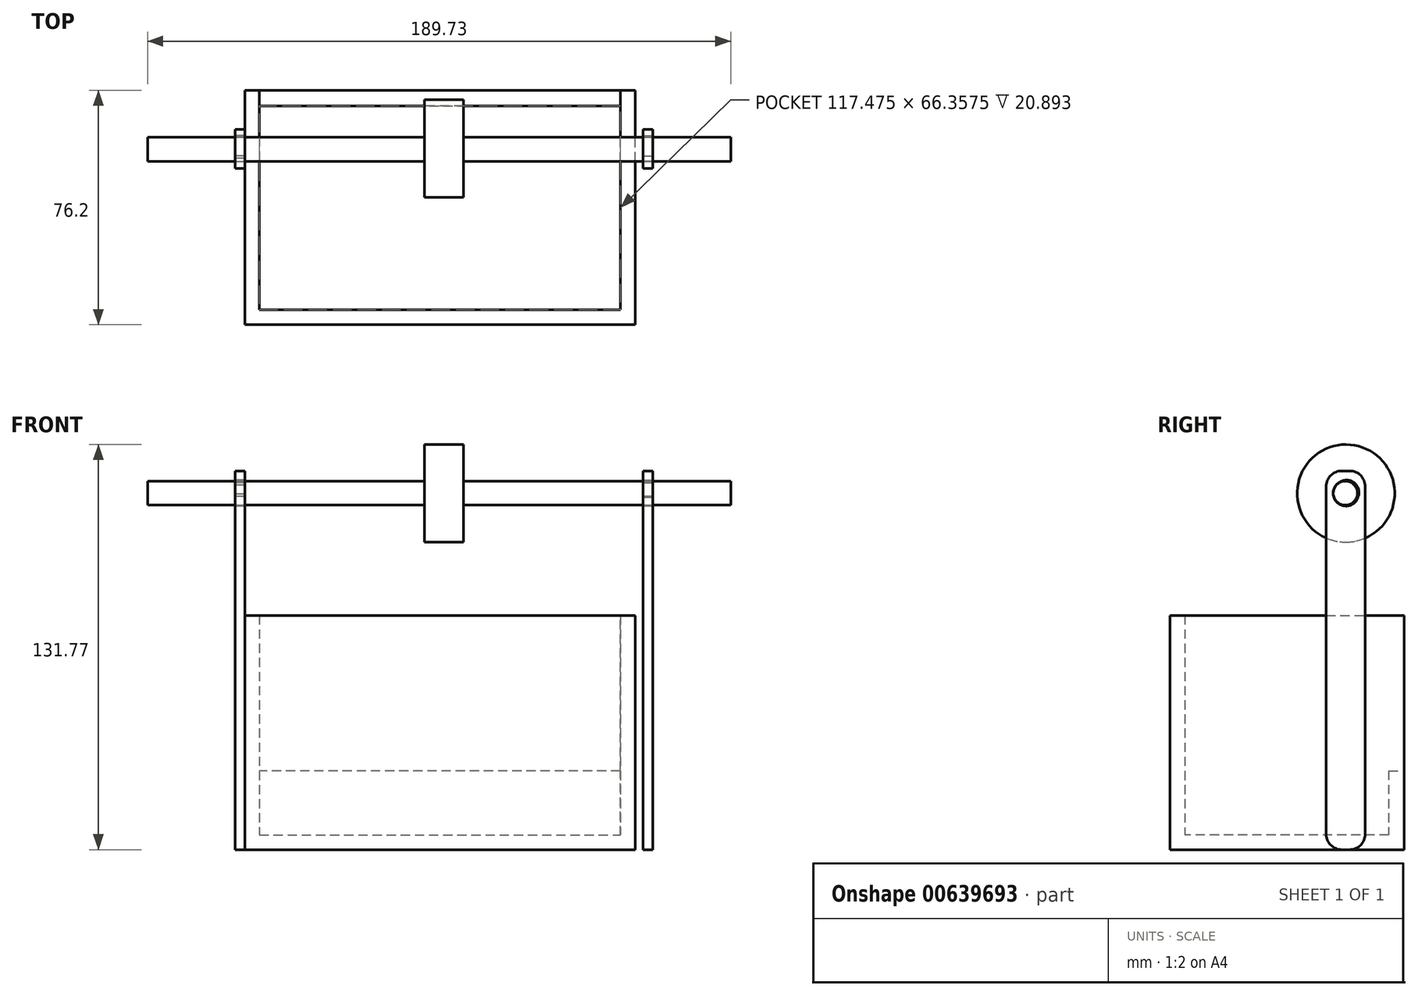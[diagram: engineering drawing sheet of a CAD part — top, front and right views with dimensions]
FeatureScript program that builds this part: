
annotation { "Feature Type Name" : "Feature", "Feature Type Description" : "" }
export const myFeature = defineFeature(function(context is Context, id is Id, definition is map)
    precondition{}
    {
        {
            var Q0;
            Q0=qCreatedBy(makeId("Top.planeOp"),FACE);
            var sketch = newSketch(context, id + "F0", { "sketchPlane" : qUnion([Q0])});
            skLineSegment(sketch, "E0", {"start": v(-64.77, -58.54) * mm, "end": v(62.23, -58.54) * mm});
            skLineSegment(sketch, "E1", {"start": v(62.23, -58.54) * mm, "end": v(62.23, 43.06) * mm});
            skLineSegment(sketch, "E2", {"start": v(62.23, 43.06) * mm, "end": v(-64.77, 43.06) * mm});
            skLineSegment(sketch, "E3", {"start": v(-64.77, 43.06) * mm, "end": v(-64.77, -58.54) * mm});
            skSolve(sketch);
        }
        {
            var Q0;
            Q0=makeQuery(id+"F0.imprint","IMPRINT",FACE,{"disambiguationData":[TD([[makeQuery(id+"F0.imprint","IMPRINT",EDGE,{"derivedFrom":sQuery(id+"F0.wireOp",EDGE,"E0")}),1.0]])]});
            extrude(context, id + "F1", {"entities" : qUnion([Q0]), "depth" : 76.2 * mm, "offsetDistance" : 25.4 * mm});
        }
        {
            var Q0;
            Q0=makeQuery(id+"F1.opExtrude","CAP_FACE",FACE,{"disambiguationData":[OSD([sQuery(id+"F0.wireOp",EDGE,"E0"),sQuery(id+"F0.wireOp",EDGE,"E1"),sQuery(id+"F0.wireOp",EDGE,"E2"),sQuery(id+"F0.wireOp",EDGE,"E3")])],"isStart":false});
            shell(context, id + "F2", {"entities" : qUnion([Q0]), "thickness" : 4.76 * mm});
        }
        {
            var Q0;
            Q0=makeQuery(id+"F1.opExtrude","CAP_FACE",FACE,{"disambiguationData":[OSD([sQuery(id+"F0.wireOp",EDGE,"E0"),sQuery(id+"F0.wireOp",EDGE,"E1"),sQuery(id+"F0.wireOp",EDGE,"E2"),sQuery(id+"F0.wireOp",EDGE,"E3")])],"isStart":true});
            var sketch = newSketch(context, id + "F3", { "sketchPlane" : qUnion([Q0])});
            skLineSegment(sketch, "E4.bottom", {"start": v(-64.77, 7.74) * mm, "end": v(-67.94, 7.74) * mm});
            skLineSegment(sketch, "E4.top", {"start": v(-64.77, -4.96) * mm, "end": v(-67.94, -4.96) * mm});
            skLineSegment(sketch, "E4.left", {"start": v(-64.77, 7.74) * mm, "end": v(-64.77, -4.96) * mm});
            skLineSegment(sketch, "E4.right", {"start": v(-67.94, 7.74) * mm, "end": v(-67.94, -4.96) * mm});
            skSolve(sketch);
        }
        {
            var Q0;
            Q0=makeQuery(id+"F3.imprint","IMPRINT",FACE,{"disambiguationData":[TD([[makeQuery(id+"F3.imprint","IMPRINT",EDGE,{"derivedFrom":sQuery(id+"F3.wireOp",EDGE,"E4.bottom")}),1.0]])]});
            extrude(context, id + "F4", {"entities" : qUnion([Q0]), "oppositeDirection" : true, "depth" : 123.19 * mm, "offsetDistance" : 25.4 * mm});
        }
        {
            var Q0;
            Q0=makeQuery(id+"F4.opExtrude","CAP_EDGE",EDGE,{"disambiguationData":[OSD([sQuery(id+"F3.wireOp",EDGE,"E4.bottom")])],"isStart":false});
            var Q1;
            Q1=makeQuery(id+"F4.opExtrude","CAP_EDGE",EDGE,{"disambiguationData":[OSD([sQuery(id+"F3.wireOp",EDGE,"E4.top")])],"isStart":false});
            var Q2;
            Q2=makeQuery(id+"F4.opExtrude","CAP_EDGE",EDGE,{"disambiguationData":[OSD([sQuery(id+"F3.wireOp",EDGE,"E4.bottom")])],"isStart":true});
            var Q3;
            Q3=makeQuery(id+"F4.opExtrude","CAP_EDGE",EDGE,{"disambiguationData":[OSD([sQuery(id+"F3.wireOp",EDGE,"E4.top")])],"isStart":true});
            fillet(context, id + "F5", {"entities" : qUnion([Q0, Q1, Q2, Q3]), "radius" : 5.08 * mm, "tangentPropagation" : true, "allowEdgeOverflow" : false});
        }
        {
            var Q0;
            Q0=makeQuery(id+"F4.opExtrude","SWEPT_FACE",FACE,{"disambiguationData":[OSD([sQuery(id+"F3.wireOp",EDGE,"E4.right")])]});
            var sketch = newSketch(context, id + "F6", { "sketchPlane" : qUnion([Q0])});
            skCircle(sketch, "E5", {"center": v(1.13, 116.18) * mm, "radius": 4.02 * mm});
            skSolve(sketch);
        }
        {
            var Q0;
            Q0=makeQuery(id+"F6.imprint","IMPRINT",FACE,{"disambiguationData":[TD([[makeQuery(id+"F6.imprint","IMPRINT",EDGE,{"derivedFrom":sQuery(id+"F6.wireOp",EDGE,"E5")}),1.0]])]});
            extrude(context, id + "F7", {"entities" : qUnion([Q0]), "operationType" : NewBodyOperationType.REMOVE, "oppositeDirection" : true, "depth" : 25.4 * mm, "offsetDistance" : 25.4 * mm});
        }
        {
            var Q0;
            Q0=makeQuery(id+"F4.opExtrude","SWEPT_BODY",BODY,{"disambiguationData":[OSD([sQuery(id+"F3.wireOp",EDGE,"E4.bottom"),sQuery(id+"F3.wireOp",EDGE,"E4.top"),sQuery(id+"F3.wireOp",EDGE,"E4.left"),sQuery(id+"F3.wireOp",EDGE,"E4.right")])]});
            var Q1;
            Q1=qCreatedBy(makeId("Right.planeOp"),FACE);
            mirror(context, id + "F8", {"entities" : qUnion([Q0]), "mirrorPlane" : qUnion([Q1])});
        }
        {
            var Q0;
            Q0=makeQuery(id+"F4.opExtrude","SWEPT_FACE",FACE,{"disambiguationData":[OSD([sQuery(id+"F3.wireOp",EDGE,"E4.right")])]});
            var sketch = newSketch(context, id + "F9", { "sketchPlane" : qUnion([Q0])});
            skCircle(sketch, "E6", {"center": v(1.33, 115.9) * mm, "radius": 4.13 * mm});
            skSolve(sketch);
        }
        {
            var Q0;
            Q0=makeQuery(id+"F9.imprint","IMPRINT",FACE,{"disambiguationData":[TD([[makeQuery(id+"F9.imprint","IMPRINT",EDGE,{"derivedFrom":sQuery(id+"F9.wireOp",EDGE,"E6")}),1.0]])]});
            extrude(context, id + "F10", {"entities" : qUnion([Q0]), "operationType" : NewBodyOperationType.REMOVE, "oppositeDirection" : true, "depth" : 137.92 * mm, "offsetDistance" : 25.4 * mm});
        }
        {
            var Q0;
            Q0=makeQuery(id+"F8.opPattern","COPY",FACE,{"derivedFrom":makeQuery(id+"F4.opExtrude","SWEPT_FACE",FACE,{"disambiguationData":[OSD([sQuery(id+"F3.wireOp",EDGE,"E4.right")])]}),"instanceName":"1"});
            var sketch = newSketch(context, id + "F11", { "sketchPlane" : qUnion([Q0])});
            skCircle(sketch, "E7", {"center": v(-1.52, 115.97) * mm, "radius": 3.96 * mm});
            skSolve(sketch);
        }
        {
            var Q0;
            Q0=makeQuery(id+"F11.imprint","IMPRINT",FACE,{"disambiguationData":[TD([[makeQuery(id+"F11.imprint","IMPRINT",EDGE,{"derivedFrom":sQuery(id+"F11.wireOp",EDGE,"E7")}),1.0]])]});
            extrude(context, id + "F12", {"entities" : qUnion([Q0]), "operationType" : NewBodyOperationType.REMOVE, "oppositeDirection" : true, "depth" : 25.4 * mm, "offsetDistance" : 25.4 * mm});
        }
        {
            var Q0;
            Q0=makeQuery(id+"F8.opPattern","COPY",FACE,{"derivedFrom":makeQuery(id+"F4.opExtrude","SWEPT_FACE",FACE,{"disambiguationData":[OSD([sQuery(id+"F3.wireOp",EDGE,"E4.right")])]}),"instanceName":"1"});
            var sketch = newSketch(context, id + "F13", { "sketchPlane" : qUnion([Q0])});
            skCircle(sketch, "E8", {"center": v(-1.52, 115.97) * mm, "radius": 3.93 * mm});
            skSolve(sketch);
        }
        {
            var Q0;
            Q0=makeQuery(id+"F13.imprint","IMPRINT",FACE,{"disambiguationData":[TD([[makeQuery(id+"F13.imprint","IMPRINT",EDGE,{"derivedFrom":sQuery(id+"F13.wireOp",EDGE,"E8")}),1.0]])]});
            extrude(context, id + "F14", {"entities" : qUnion([Q0]), "operationType" : NewBodyOperationType.ADD, "oppositeDirection" : true, "depth" : 164.34 * mm, "offsetDistance" : 25.4 * mm});
        }
        {
            var Q0;
            Q0=makeQuery(id+"F14.opExtrude","CAP_FACE",FACE,{"disambiguationData":[OSD([sQuery(id+"F13.wireOp",EDGE,"E8")])],"isStart":true});
            extrude(context, id + "F15", {"entities" : qUnion([Q0]), "operationType" : NewBodyOperationType.ADD, "depth" : 25.4 * mm, "offsetDistance" : 25.4 * mm});
        }
        {
            var Q0;
            Q0=makeQuery(id+"F1.opExtrude","SWEPT_FACE",FACE,{"disambiguationData":[OSD([sQuery(id+"F0.wireOp",EDGE,"E2")])]});
            extrude(context, id + "F16", {"entities" : qUnion([Q0]), "operationType" : NewBodyOperationType.REMOVE, "oppositeDirection" : true, "depth" : 25.4 * mm, "offsetDistance" : 25.4 * mm});
        }
        {
            var Q0;
            Q0=makeQuery(id+"F16.boolean.opBoolean","COPY",FACE,{"derivedFrom":makeQuery(id+"F16.opExtrude","CAP_FACE",FACE,{"disambiguationData":[OSD([sQuery(id+"F0.wireOp",EDGE,"E2")])],"isStart":false})});
            var sketch = newSketch(context, id + "F17", { "sketchPlane" : qUnion([Q0])});
            skLineSegment(sketch, "E9.bottom", {"start": v(-57.47, 25.66) * mm, "end": v(60, 25.66) * mm});
            skLineSegment(sketch, "E9.top", {"start": v(-57.47, 4.76) * mm, "end": v(60, 4.76) * mm});
            skLineSegment(sketch, "E9.left", {"start": v(-57.47, 25.66) * mm, "end": v(-57.47, 4.76) * mm});
            skLineSegment(sketch, "E9.right", {"start": v(60, 25.66) * mm, "end": v(60, 4.76) * mm});
            skSolve(sketch);
        }
        {
            var Q0;
            Q0=makeQuery(id+"F17.imprint","IMPRINT",FACE,{"disambiguationData":[TD([[makeQuery(id+"F17.imprint","IMPRINT",EDGE,{"derivedFrom":sQuery(id+"F17.wireOp",EDGE,"E9.bottom")}),-1.0]])]});
            extrude(context, id + "F18", {"entities" : qUnion([Q0]), "operationType" : NewBodyOperationType.ADD, "oppositeDirection" : true, "depth" : 5.08 * mm, "offsetDistance" : 25.4 * mm});
        }
        {
            var Q0;
            Q0=qCreatedBy(makeId("Right.planeOp"),FACE);
            var sketch = newSketch(context, id + "F19", { "sketchPlane" : qUnion([Q0])});
            skArc(sketch, "E10.0", {"start": v(-5.45, 115.72) * mm, "mid": v(2.54, 114.45) * mm, "end": v(-4.33, 118.73) * mm});
            skCircle(sketch, "E11", {"center": v(-1.33, 115.9) * mm, "radius": 15.88 * mm});
            skSolve(sketch);
        }
        {
            var Q0;
            Q0=makeQuery(id+"F19.imprint","IMPRINT",FACE,{"disambiguationData":[TD([[makeQuery(id+"F19.imprint","IMPRINT",EDGE,{"derivedFrom":sQuery(id+"F19.wireOp",EDGE,"E11")}),1.0]])]});
            extrude(context, id + "F20", {"entities" : qUnion([Q0]), "operationType" : NewBodyOperationType.ADD, "endBound" : BoundingType.SYMMETRIC, "depth" : 12.7 * mm, "offsetDistance" : 25.4 * mm});
        }
    });
